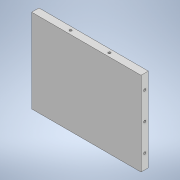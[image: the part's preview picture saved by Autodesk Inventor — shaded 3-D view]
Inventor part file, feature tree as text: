
AUTODESK INVENTOR PART (.ipt)
format: ipt  version: 2022.2 (Build 262287030, 287C)  size: 132,608 bytes
history: native  units: in
note: dims shown in document units (in); Inventor stores cm internally (conversion verified against a paired STEP export)
features: sketch x5, hole x4, extrude x1
ambient origin geometry x8: Origin, YZ Plane, XZ Plane, XY Plane, X Axis, Y Axis, Z Axis, Center Point
bodies: Solid1 (feature_tree)
feature tree (10):
  extrude  "Extrusion1"  Depth=4.5276in
  hole  "Hole1"  [1 undecoded]
  hole  "Hole2"  [1 undecoded]
  hole  "Hole3"  [1 undecoded]
  hole  "Hole4"  [1 undecoded]
  sketch  "Sketch1"  dims[d0=5.9055in d1=4.5276in]
  sketch  "Sketch2"  dims[d2=0.3937in d3=0.0in d4=0.7874in]
  sketch  "Sketch3"  dims[d5=0.1969in d6=1.1811in d8=1.4764in d9=0.3937in d11=0.3937in]
  sketch  "Sketch4"  dims[d13=0.125in d14=0.2953in d15=0.1476in d16=0.0984in d17=90.0deg d18=0.1969in d19=0.0in d21=0.1969in]
  sketch  "Sketch5"  dims[d22=0.7874in d24=2.0997in d25=0.3937in d27=0.3937in d29=0.125in d30=0.2953in d31=0.1476in d32=0.0984in d33=90.0deg d34=0.1969in d35=0.0in d37=0.1969in d38=0.7874in d40=2.1654in d41=0.3937in d43=0.3937in d45=0.125in d46=0.2953in d47=0.1476in d48=0.0984in d49=90.0deg d50=0.1969in d51=0.0in d52=0.7874in d53=0.1969in d54=1.1811in d56=1.4764in d57=0.3937in d59=0.3937in d61=0.125in d62=0.2953in d63=0.1476in d64=0.0984in d65=90.0deg d66=0.1969in d67=0.0in d68=1.0827in d69=1.0499in d70=0.3937in d71=0.3937in d72=0.0591in d73=0.0984in d74=0.1476in d75=0.5635in d76=0.2953in d77=0.8108in d78=0.0246in d79=0.2953in d80=0.1476in]
note: 4 required parameter values undecoded (feature->parameter linkage not recoverable at this tier; creation-order binding heuristic only, values carry confidence <= 0.55)
